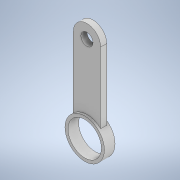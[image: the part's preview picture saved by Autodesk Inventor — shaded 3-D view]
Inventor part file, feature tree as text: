
AUTODESK INVENTOR PART (.ipt)
format: ipt  version: 2021 (Build 250183000, 183)  size: 128,512 bytes
history: native  units: mm
features: extrude x3, sketch x3, plane x1, fillet x1
ambient origin geometry x8: Origin, YZ Plane, XZ Plane, XY Plane, X Axis, Y Axis, Z Axis, Center Point
bodies: Solid1 (feature_tree)
feature tree (8):
  extrude  "Extrusion1"  Depth=26.0mm
  plane  "Work Plane1"
  extrude  "Extrusion2"  Depth=7.0mm
  fillet  "Fillet1"  Radius=65.0mm
  extrude  "Extrusion3"  Depth=9.0mm
  sketch  "Sketch1"  dims[d0=22.0mm d1=26.0mm]
  sketch  "Sketch2"  dims[d2=7.0mm d3=0.0mm d4=3.5mm d5=65.0mm]
  sketch  "Sketch3"  dims[d6=2.0mm d7=2.0mm d8=0.0mm d9=0.0mm d10=9.0mm d11=8.0mm d13=2.0mm d14=0.0mm d15=18.0mm d17=0.0mm]
